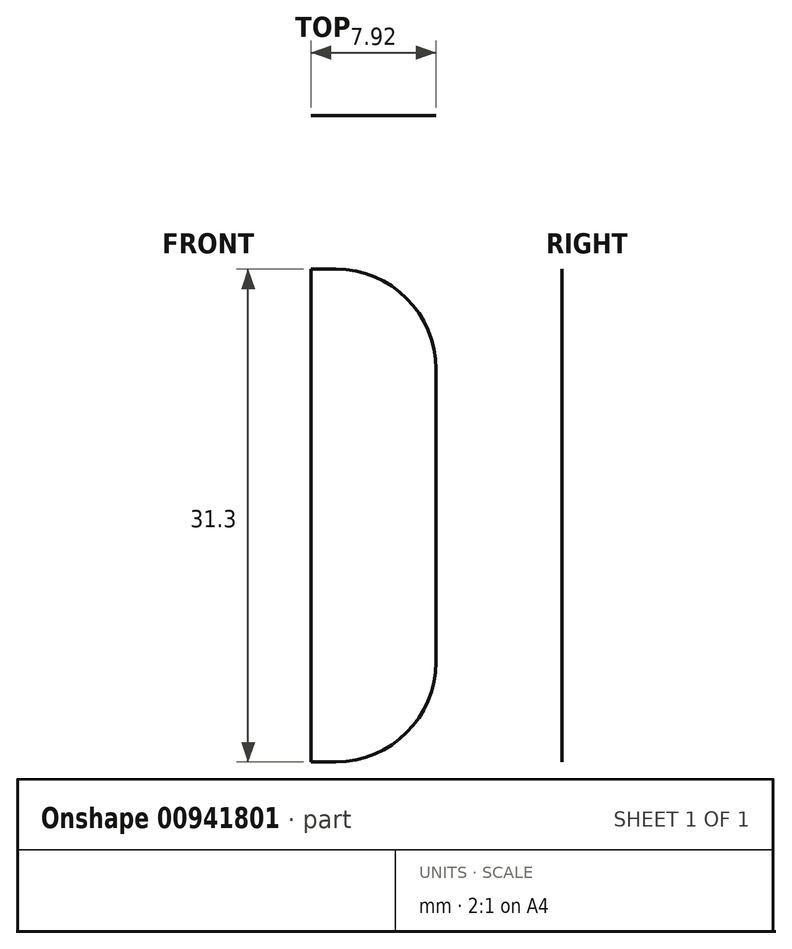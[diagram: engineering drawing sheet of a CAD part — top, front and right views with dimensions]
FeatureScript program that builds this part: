
annotation { "Feature Type Name" : "Feature", "Feature Type Description" : "" }
export const myFeature = defineFeature(function(context is Context, id is Id, definition is map)
    precondition{}
    {
        {
            var Q0;
            Q0=qCreatedBy(makeId("Front.planeOp"),FACE);
            var sketch = newSketch(context, id + "F0", { "sketchPlane" : qUnion([Q0])});
            skLineSegment(sketch, "E0.bottom", {"start": v(0, 0) * mm, "end": v(1.57, 0) * mm});
            skLineSegment(sketch, "E0.top", {"start": v(0, -31.3) * mm, "end": v(1.57, -31.3) * mm});
            skLineSegment(sketch, "E0.left", {"start": v(0, 0) * mm, "end": v(0, -31.3) * mm});
            skLineSegment(sketch, "E0.right", {"start": v(7.92, -6.35) * mm, "end": v(7.92, -24.95) * mm});
            skPoint(sketch, "E1.visualSharp", {"position": v(7.92, 0) * mm});
            skArc(sketch, "E1.filletArc", {"start": v(7.92, -6.35) * mm, "mid": v(6.06, -1.86) * mm, "end": v(1.57, 0) * mm});
            skPoint(sketch, "E2.visualSharp", {"position": v(7.92, -31.3) * mm});
            skArc(sketch, "E2.filletArc", {"start": v(1.57, -31.3) * mm, "mid": v(6.06, -29.44) * mm, "end": v(7.92, -24.95) * mm});
            skSolve(sketch);
        }
        {
            var Q0;
            Q0 = qSketchRegion(id + "F0", true);
            extrude(context, id + "F1", {"entities" : qUnion([Q0]), "depth" : 0 * mm, "offsetDistance" : 25.4 * mm});
        }
    });
